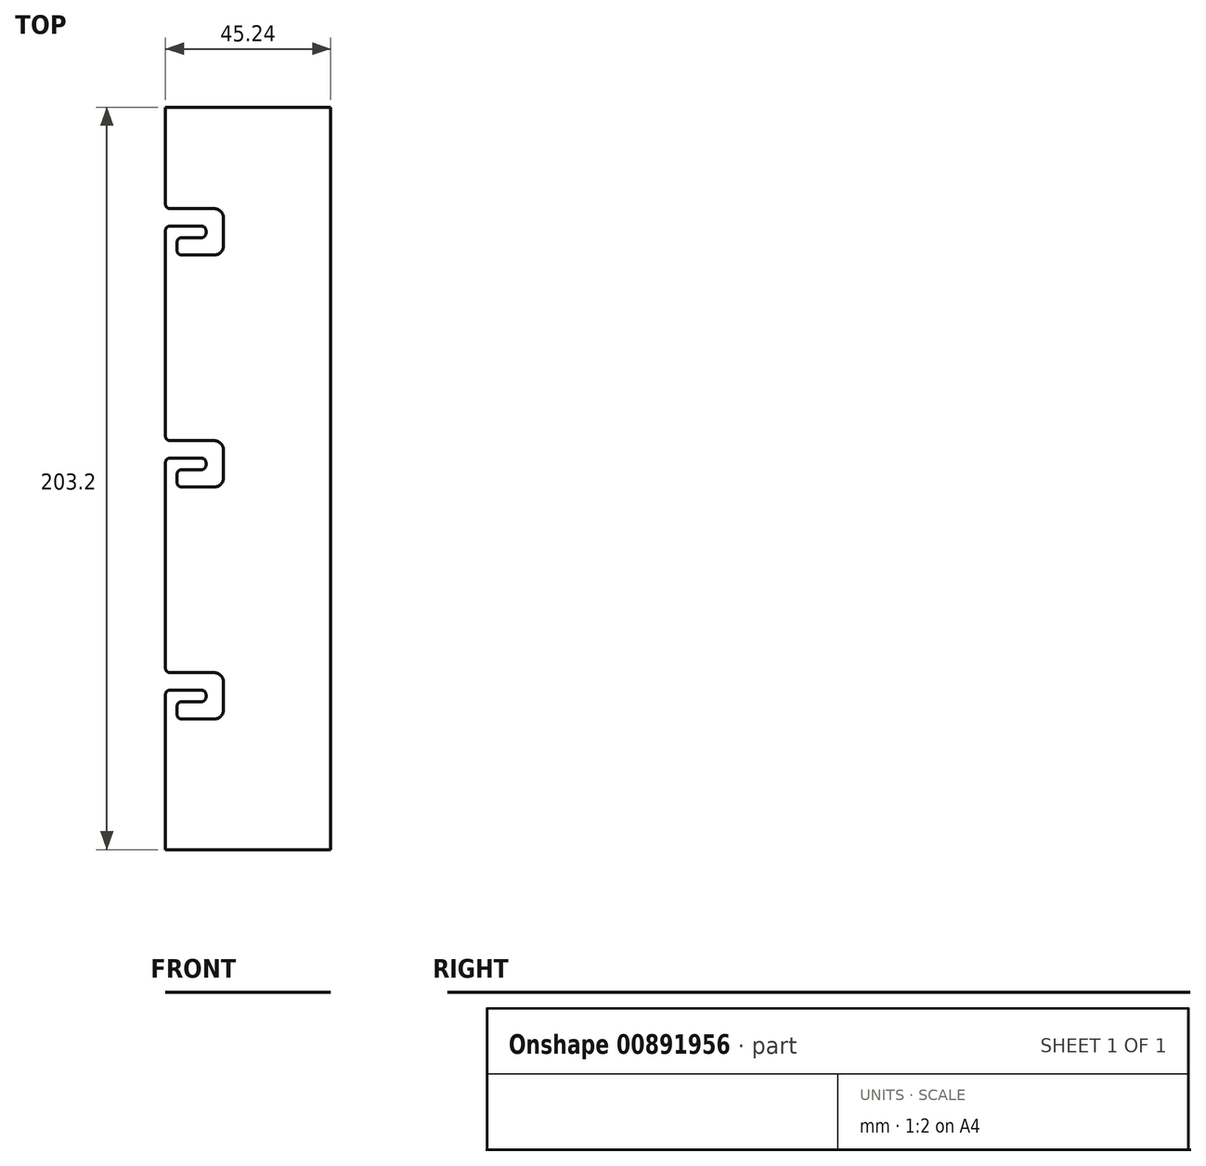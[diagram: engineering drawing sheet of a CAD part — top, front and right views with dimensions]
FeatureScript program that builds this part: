
annotation { "Feature Type Name" : "Feature", "Feature Type Description" : "" }
export const myFeature = defineFeature(function(context is Context, id is Id, definition is map)
    precondition{}
    {
        {
            var Q0;
            Q0=qCreatedBy(makeId("Top.planeOp"),FACE);
            var sketch = newSketch(context, id + "F0", { "sketchPlane" : qUnion([Q0])});
            skLineSegment(sketch, "E0.bottom", {"start": v(0, 203.2) * mm, "end": v(-45.24, 203.2) * mm});
            skLineSegment(sketch, "E0.top", {"start": v(0, 0) * mm, "end": v(-45.24, 0) * mm});
            skLineSegment(sketch, "E0.left", {"start": v(0, 203.2) * mm, "end": v(0, 0) * mm});
            skLineSegment(sketch, "E0.right", {"start": v(-45.24, 203.2) * mm, "end": v(-45.24, 176.69) * mm});
            skPoint(sketch, "E0.middle", {"position": v(0, 0) * mm});
            skLineSegment(sketch, "E1", {"start": v(-43.97, 48.42) * mm, "end": v(-31.9, 48.42) * mm});
            skLineSegment(sketch, "E2", {"start": v(-29.37, 45.88) * mm, "end": v(-29.37, 38.26) * mm});
            skLineSegment(sketch, "E3", {"start": v(-31.9, 35.72) * mm, "end": v(-40.8, 35.72) * mm});
            skLineSegment(sketch, "E4", {"start": v(-42.07, 36.99) * mm, "end": v(-42.07, 39.21) * mm});
            skLineSegment(sketch, "E5", {"start": v(-40.8, 40.48) * mm, "end": v(-35.4, 40.48) * mm});
            skLineSegment(sketch, "E6", {"start": v(-34.13, 41.75) * mm, "end": v(-34.13, 42.39) * mm});
            skLineSegment(sketch, "E7", {"start": v(-35.4, 43.66) * mm, "end": v(-43.97, 43.66) * mm});
            skPoint(sketch, "E8.visualSharp", {"position": v(-29.37, 48.42) * mm});
            skArc(sketch, "E8.filletArc", {"start": v(-29.37, 45.88) * mm, "mid": v(-30.11, 47.67) * mm, "end": v(-31.9, 48.42) * mm});
            skPoint(sketch, "E9.visualSharp", {"position": v(-34.13, 43.66) * mm});
            skArc(sketch, "E9.filletArc", {"start": v(-34.13, 42.39) * mm, "mid": v(-34.5, 43.28) * mm, "end": v(-35.4, 43.66) * mm});
            skPoint(sketch, "E10.visualSharp", {"position": v(-42.07, 40.48) * mm});
            skArc(sketch, "E10.filletArc", {"start": v(-40.8, 40.48) * mm, "mid": v(-41.7, 40.1) * mm, "end": v(-42.07, 39.21) * mm});
            skPoint(sketch, "E11.visualSharp", {"position": v(-42.07, 35.72) * mm});
            skArc(sketch, "E11.filletArc", {"start": v(-42.07, 36.99) * mm, "mid": v(-41.7, 36.1) * mm, "end": v(-40.8, 35.72) * mm});
            skPoint(sketch, "E12.visualSharp", {"position": v(-34.13, 40.48) * mm});
            skArc(sketch, "E12.filletArc", {"start": v(-35.4, 40.48) * mm, "mid": v(-34.5, 40.85) * mm, "end": v(-34.13, 41.75) * mm});
            skPoint(sketch, "E13.visualSharp", {"position": v(-29.37, 35.72) * mm});
            skArc(sketch, "E13.filletArc", {"start": v(-31.9, 35.72) * mm, "mid": v(-30.11, 36.46) * mm, "end": v(-29.37, 38.26) * mm});
            skPoint(sketch, "E14.0.1.0", {"position": v(-29.37, 111.92) * mm});
            skPoint(sketch, "E14.0.1.1", {"position": v(-29.37, 99.22) * mm});
            skLineSegment(sketch, "E14.0.1.2", {"start": v(-29.37, 109.38) * mm, "end": v(-29.37, 101.76) * mm});
            skLineSegment(sketch, "E14.0.1.3", {"start": v(-31.9, 99.22) * mm, "end": v(-40.8, 99.22) * mm});
            skPoint(sketch, "E14.0.1.4", {"position": v(-34.13, 103.98) * mm});
            skLineSegment(sketch, "E14.0.1.5", {"start": v(-43.97, 111.92) * mm, "end": v(-31.9, 111.92) * mm});
            skPoint(sketch, "E14.0.1.6", {"position": v(-42.07, 99.22) * mm});
            skPoint(sketch, "E14.0.1.7", {"position": v(-34.13, 107.16) * mm});
            skPoint(sketch, "E14.0.1.8", {"position": v(-42.07, 103.98) * mm});
            skArc(sketch, "E14.0.1.9", {"start": v(-31.9, 99.22) * mm, "mid": v(-30.11, 99.96) * mm, "end": v(-29.37, 101.76) * mm});
            skLineSegment(sketch, "E14.0.1.11", {"start": v(-35.4, 107.16) * mm, "end": v(-43.97, 107.16) * mm});
            skArc(sketch, "E14.0.1.12", {"start": v(-29.37, 109.38) * mm, "mid": v(-30.11, 111.17) * mm, "end": v(-31.9, 111.92) * mm});
            skArc(sketch, "E14.0.1.13", {"start": v(-35.4, 103.98) * mm, "mid": v(-34.5, 104.35) * mm, "end": v(-34.13, 105.25) * mm});
            skArc(sketch, "E14.0.1.14", {"start": v(-42.07, 100.49) * mm, "mid": v(-41.7, 99.6) * mm, "end": v(-40.8, 99.22) * mm});
            skArc(sketch, "E14.0.1.15", {"start": v(-34.13, 105.89) * mm, "mid": v(-34.5, 106.78) * mm, "end": v(-35.4, 107.16) * mm});
            skLineSegment(sketch, "E14.0.1.16", {"start": v(-40.8, 103.98) * mm, "end": v(-35.4, 103.98) * mm});
            skLineSegment(sketch, "E14.0.1.17", {"start": v(-42.07, 100.49) * mm, "end": v(-42.07, 102.71) * mm});
            skLineSegment(sketch, "E14.0.1.18", {"start": v(-34.13, 105.25) * mm, "end": v(-34.13, 105.89) * mm});
            skArc(sketch, "E14.0.1.19", {"start": v(-40.8, 103.98) * mm, "mid": v(-41.7, 103.6) * mm, "end": v(-42.07, 102.71) * mm});
            skPoint(sketch, "E14.0.2.0", {"position": v(-29.37, 175.42) * mm});
            skPoint(sketch, "E14.0.2.1", {"position": v(-29.37, 162.72) * mm});
            skLineSegment(sketch, "E14.0.2.2", {"start": v(-29.37, 172.88) * mm, "end": v(-29.37, 165.26) * mm});
            skLineSegment(sketch, "E14.0.2.3", {"start": v(-31.9, 162.72) * mm, "end": v(-40.8, 162.72) * mm});
            skPoint(sketch, "E14.0.2.4", {"position": v(-34.13, 167.48) * mm});
            skLineSegment(sketch, "E14.0.2.5", {"start": v(-43.97, 175.42) * mm, "end": v(-31.9, 175.42) * mm});
            skPoint(sketch, "E14.0.2.6", {"position": v(-42.07, 162.72) * mm});
            skPoint(sketch, "E14.0.2.7", {"position": v(-34.13, 170.66) * mm});
            skPoint(sketch, "E14.0.2.8", {"position": v(-42.07, 167.48) * mm});
            skArc(sketch, "E14.0.2.9", {"start": v(-31.9, 162.72) * mm, "mid": v(-30.11, 163.46) * mm, "end": v(-29.37, 165.26) * mm});
            skLineSegment(sketch, "E14.0.2.11", {"start": v(-35.4, 170.66) * mm, "end": v(-43.97, 170.66) * mm});
            skArc(sketch, "E14.0.2.12", {"start": v(-29.37, 172.88) * mm, "mid": v(-30.11, 174.67) * mm, "end": v(-31.9, 175.42) * mm});
            skArc(sketch, "E14.0.2.13", {"start": v(-35.4, 167.48) * mm, "mid": v(-34.5, 167.85) * mm, "end": v(-34.13, 168.75) * mm});
            skArc(sketch, "E14.0.2.14", {"start": v(-42.07, 163.99) * mm, "mid": v(-41.7, 163.1) * mm, "end": v(-40.8, 162.72) * mm});
            skArc(sketch, "E14.0.2.15", {"start": v(-34.13, 169.39) * mm, "mid": v(-34.5, 170.28) * mm, "end": v(-35.4, 170.66) * mm});
            skLineSegment(sketch, "E14.0.2.16", {"start": v(-40.8, 167.48) * mm, "end": v(-35.4, 167.48) * mm});
            skLineSegment(sketch, "E14.0.2.17", {"start": v(-42.07, 163.99) * mm, "end": v(-42.07, 166.21) * mm});
            skLineSegment(sketch, "E14.0.2.18", {"start": v(-34.13, 168.75) * mm, "end": v(-34.13, 169.39) * mm});
            skArc(sketch, "E14.0.2.19", {"start": v(-40.8, 167.48) * mm, "mid": v(-41.7, 167.1) * mm, "end": v(-42.07, 166.21) * mm});
            skLineSegment(sketch, "E14.direction1", {"start": v(-42.07, 38.9) * mm, "end": v(25.75, 38.9) * mm, "construction": true});
            skLineSegment(sketch, "E14.direction2", {"start": v(-42.07, 38.9) * mm, "end": v(-42.07, 102.4) * mm, "construction": true});
            skLineSegment(sketch, "E15.trimOffspring", {"start": v(-45.24, 169.39) * mm, "end": v(-45.24, 113.19) * mm});
            skLineSegment(sketch, "E16.trimOffspring", {"start": v(-45.24, 105.89) * mm, "end": v(-45.24, 49.69) * mm});
            skLineSegment(sketch, "E17.trimOffspring", {"start": v(-45.24, 42.39) * mm, "end": v(-45.24, 0) * mm});
            skPoint(sketch, "E18.visualSharp", {"position": v(-45.24, 48.42) * mm});
            skArc(sketch, "E18.filletArc", {"start": v(-45.24, 49.69) * mm, "mid": v(-44.87, 48.8) * mm, "end": v(-43.97, 48.42) * mm});
            skPoint(sketch, "E19.visualSharp", {"position": v(-45.24, 43.66) * mm});
            skArc(sketch, "E19.filletArc", {"start": v(-43.97, 43.66) * mm, "mid": v(-44.87, 43.28) * mm, "end": v(-45.24, 42.39) * mm});
            skPoint(sketch, "E20.visualSharp", {"position": v(-45.24, 107.16) * mm});
            skArc(sketch, "E20.filletArc", {"start": v(-43.97, 107.16) * mm, "mid": v(-44.87, 106.78) * mm, "end": v(-45.24, 105.89) * mm});
            skPoint(sketch, "E21.visualSharp", {"position": v(-45.24, 111.92) * mm});
            skArc(sketch, "E21.filletArc", {"start": v(-45.24, 113.19) * mm, "mid": v(-44.87, 112.3) * mm, "end": v(-43.97, 111.92) * mm});
            skPoint(sketch, "E22.visualSharp", {"position": v(-45.24, 170.66) * mm});
            skArc(sketch, "E22.filletArc", {"start": v(-43.97, 170.66) * mm, "mid": v(-44.87, 170.28) * mm, "end": v(-45.24, 169.39) * mm});
            skPoint(sketch, "E23.visualSharp", {"position": v(-45.24, 175.42) * mm});
            skArc(sketch, "E23.filletArc", {"start": v(-45.24, 176.69) * mm, "mid": v(-44.87, 175.8) * mm, "end": v(-43.97, 175.42) * mm});
            skSolve(sketch);
        }
        {
            var Q0;
            Q0=makeQuery(id+"F0.imprint","IMPRINT",FACE,{"disambiguationData":[TD([[makeQuery(id+"F0.imprint","IMPRINT",EDGE,{"derivedFrom":sQuery(id+"F0.wireOp",EDGE,"E0.bottom")}),1.0]])]});
            extrude(context, id + "F1", {"entities" : qUnion([Q0]), "depth" : 1 / 203.2 * mm, "offsetDistance" : 25.4 * mm});
        }
    });
